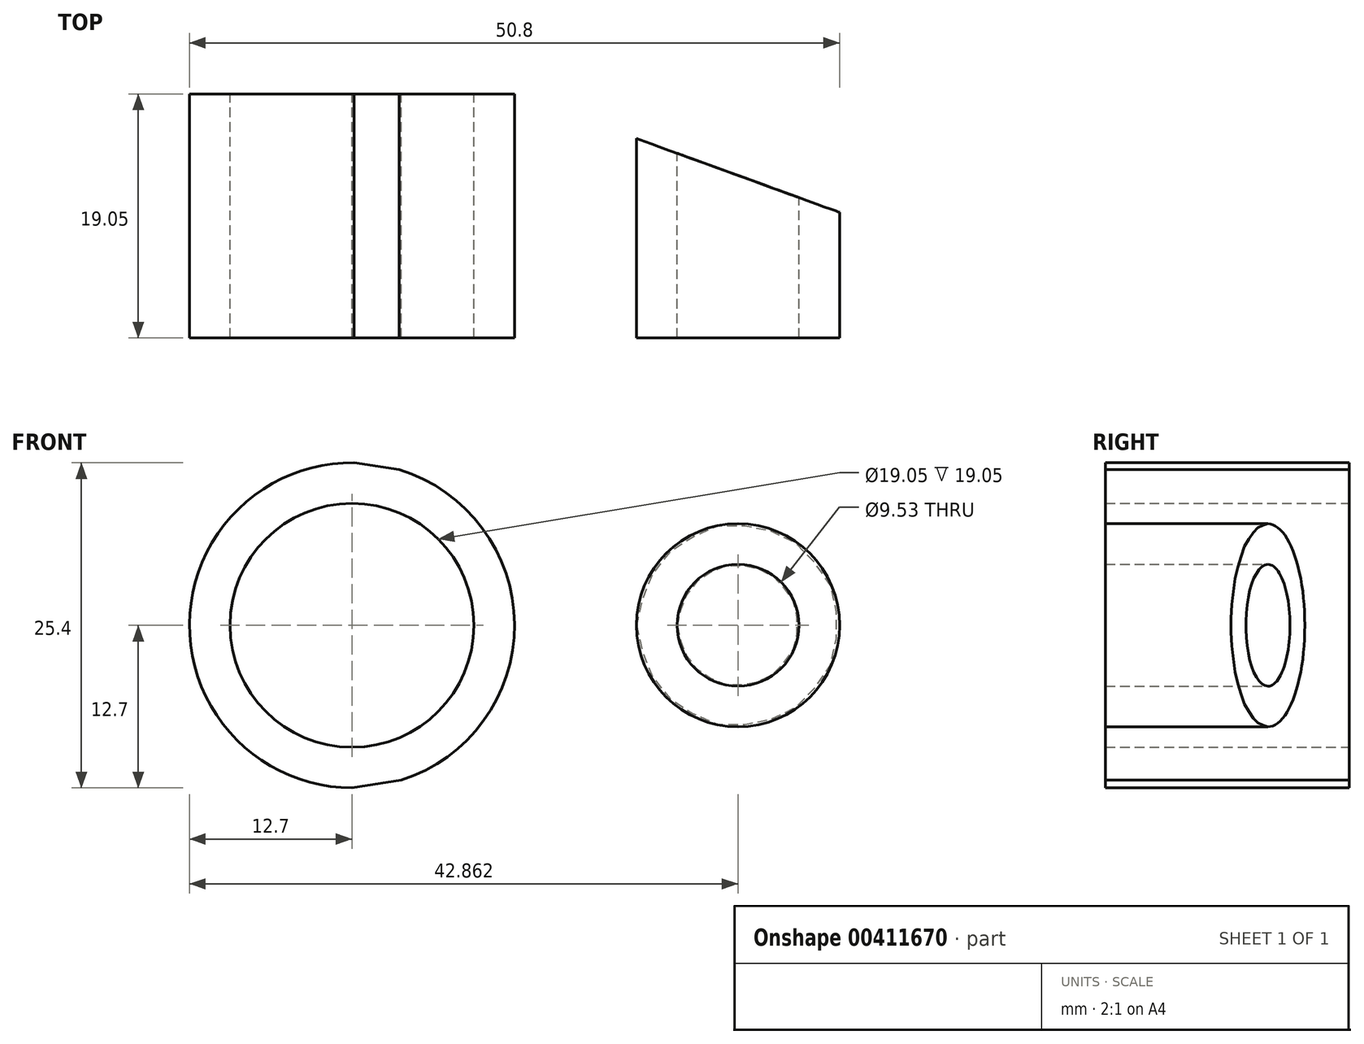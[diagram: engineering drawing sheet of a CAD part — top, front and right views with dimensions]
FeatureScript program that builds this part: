
annotation { "Feature Type Name" : "Feature", "Feature Type Description" : "" }
export const myFeature = defineFeature(function(context is Context, id is Id, definition is map)
    precondition{}
    {
        {
            var Q0;
            Q0=qCreatedBy(makeId("Front.planeOp"),FACE);
            var sketch = newSketch(context, id + "F0", { "sketchPlane" : qUnion([Q0])});
            skCircle(sketch, "E0", {"center": v(0, 0) * mm, "radius": 12.7 * mm});
            skCircle(sketch, "E1", {"center": v(30.16, 0) * mm, "radius": 7.94 * mm});
            skLineSegment(sketch, "E2", {"start": v(0, -12.7) * mm, "end": v(31.38, -7.84) * mm});
            skLineSegment(sketch, "E3", {"start": v(0.17, 12.7) * mm, "end": v(31.38, 7.84) * mm});
            skCircle(sketch, "E4", {"center": v(0, 0) * mm, "radius": 9.53 * mm});
            skCircle(sketch, "E5", {"center": v(30.16, 0) * mm, "radius": 4.76 * mm});
            skSolve(sketch);
        }
        {
            var Q0;
            {var subQ0=sQuery(id+"F0.wireOp",EDGE,"E3");var subQ1=sQuery(id+"F0.wireOp",EDGE,"E0");var subQ2=makeQuery(id+"F0.imprint","INTERSECT",VERTEX,{"disambiguationData":[OD(1.0)],"derivedFrom":[subQ1,subQ0]});Q0=makeQuery(id+"F0.imprint","IMPRINT",FACE,{"disambiguationData":[TD([[makeQuery(id+"F0.imprint","IMPRINT",EDGE,{"disambiguationData":[TD([[subQ2,1.0]])],"derivedFrom":subQ1}),-1.0]])]});}
            var Q1;
            Q1=makeQuery(id+"F0.imprint","IMPRINT",FACE,{"disambiguationData":[TD([[makeQuery(id+"F0.imprint","IMPRINT",EDGE,{"derivedFrom":sQuery(id+"F0.wireOp",EDGE,"E5")}),-1.0]])]});
            var Q2;
            Q2=makeQuery(id+"F0.imprint","IMPRINT",FACE,{"disambiguationData":[TD([[makeQuery(id+"F0.imprint","IMPRINT",EDGE,{"derivedFrom":sQuery(id+"F0.wireOp",EDGE,"E4")}),-1.0]])]});
            extrude(context, id + "F1", {"entities" : qUnion([Q0, Q1, Q2]), "depth" : 19.05 * mm});
        }
        {
            var Q0;
            Q0=qCreatedBy(makeId("Top.planeOp"),FACE);
            var sketch = newSketch(context, id + "F2", { "sketchPlane" : qUnion([Q0])});
            skLineSegment(sketch, "E6", {"start": v(0, 0) * mm, "end": v(12.7, 0) * mm});
            skLineSegment(sketch, "E7", {"start": v(38.1, 0) * mm, "end": v(12.7, 0) * mm});
            skLineSegment(sketch, "E8", {"start": v(38.1, -9.24) * mm, "end": v(38.1, 0) * mm});
            skLineSegment(sketch, "E9", {"start": v(38.1, -9.24) * mm, "end": v(12.7, 0) * mm});
            skLineSegment(sketch, "E10", {"start": v(38.1, 0) * mm, "end": v(38.1, -19.05) * mm});
            skSolve(sketch);
        }
        {
            var Q0;
            Q0 = qSketchRegion(id + "F2", true);
            extrude(context, id + "F3", {"entities" : qUnion([Q0]), "operationType" : NewBodyOperationType.REMOVE, "endBound" : BoundingType.THROUGH_ALL, "depth" : 26.15 * mm, "hasSecondDirection" : true, "secondDirectionBound" : SecondDirectionBoundingType.THROUGH_ALL, "secondDirectionOppositeDirection" : true, "secondDirectionDepth" : 25.4 * mm});
        }
    });
